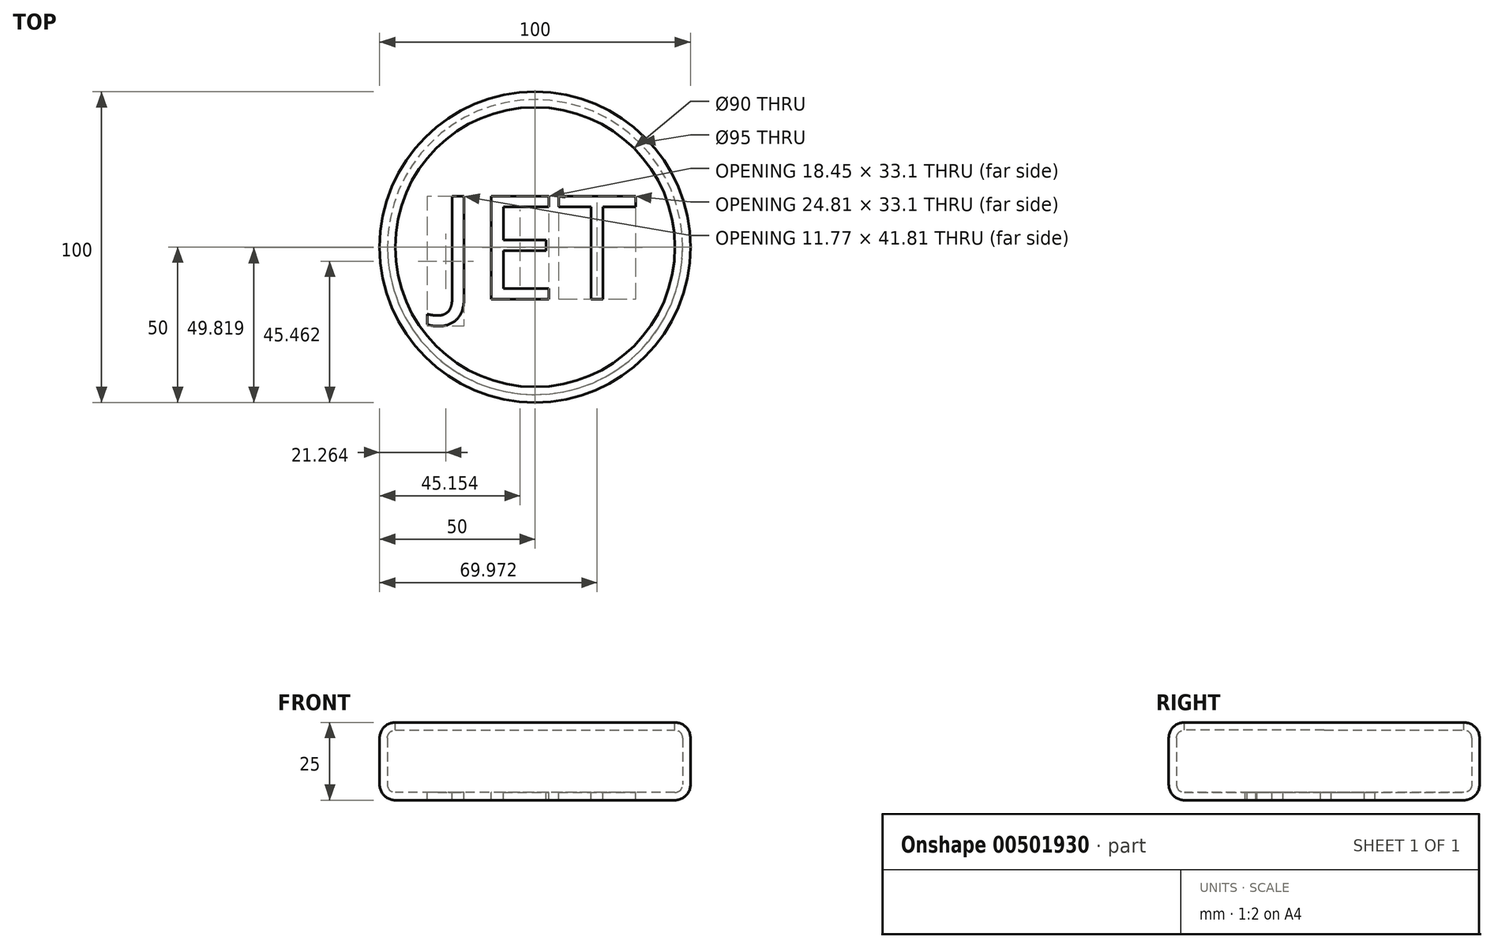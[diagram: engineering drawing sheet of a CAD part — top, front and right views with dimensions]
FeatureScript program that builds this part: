
annotation { "Feature Type Name" : "Feature", "Feature Type Description" : "" }
export const myFeature = defineFeature(function(context is Context, id is Id, definition is map)
    precondition{}
    {
        {
            var Q0;
            Q0=qCreatedBy(makeId("Top.planeOp"),FACE);
            var sketch = newSketch(context, id + "F0", { "sketchPlane" : qUnion([Q0])});
            skCircle(sketch, "E0", {"center": v(0, 0) * mm, "radius": 50 * mm});
            skSolve(sketch);
        }
        {
            var Q0;
            Q0=makeQuery(id+"F0.imprint","IMPRINT",FACE,{"disambiguationData":[TD([[makeQuery(id+"F0.imprint","IMPRINT",EDGE,{"derivedFrom":sQuery(id+"F0.wireOp",EDGE,"E0")}),1.0]])]});
            extrude(context, id + "F1", {"entities" : qUnion([Q0]), "depth" : 25 * mm});
        }
        {
            var Q0;
            Q0=makeQuery(id+"F1.opExtrude","CAP_EDGE",EDGE,{"disambiguationData":[OSD([sQuery(id+"F0.wireOp",EDGE,"E0")])],"isStart":false});
            var Q1;
            Q1=makeQuery(id+"F1.opExtrude","CAP_EDGE",EDGE,{"disambiguationData":[OSD([sQuery(id+"F0.wireOp",EDGE,"E0")])],"isStart":true});
            fillet(context, id + "F2", {"entities" : qUnion([Q0, Q1]), "radius" : 5 * mm, "tangentPropagation" : true, "allowEdgeOverflow" : false});
        }
        {
            var Q0;
            Q0=makeQuery(id+"F1.opExtrude","CAP_FACE",FACE,{"disambiguationData":[OSD([sQuery(id+"F0.wireOp",EDGE,"E0")])],"isStart":false});
            shell(context, id + "F3", {"entities" : qUnion([Q0]), "thickness" : 2.5 * mm});
        }
        {
            var Q0;
            {var subQ0=sQuery(id+"F0.wireOp",EDGE,"E0");Q0=makeQuery(id+"F3.opShell","OFFSET_FACE",FACE,{"disambiguationData":[OSD([subQ0]),TDD([makeQuery(id+"F1.opExtrude","CAP_FACE",FACE,{"disambiguationData":[OSD([subQ0])],"isStart":true})])]});}
            var sketch = newSketch(context, id + "F4", { "sketchPlane" : qUnion([Q0])});
            skText(sketch, "E1", { "text": "JET", "fontName": "OpenSans-Regular.ttf"});
            const initialGuessF4  = {"E1": [-0.031, -0.01673, 1, 0, 0.03338]};
            skSetInitialGuess(sketch, initialGuessF4);
            skSolve(sketch);
        }
        {
            var Q0;
            Q0 = qSketchRegion(id + "F4", true);
            var Q1;
            Q1=makeQuery(id+"F1.opExtrude","CAP_FACE",FACE,{"disambiguationData":[OSD([sQuery(id+"F0.wireOp",EDGE,"E0")])],"isStart":true});
            extrude(context, id + "F5", {"entities" : qUnion([Q0]), "operationType" : NewBodyOperationType.REMOVE, "endBound" : BoundingType.UP_TO_SURFACE, "oppositeDirection" : true, "endBoundEntityFace" : qUnion([Q1]), "depth" : 25 * mm});
        }
    });
